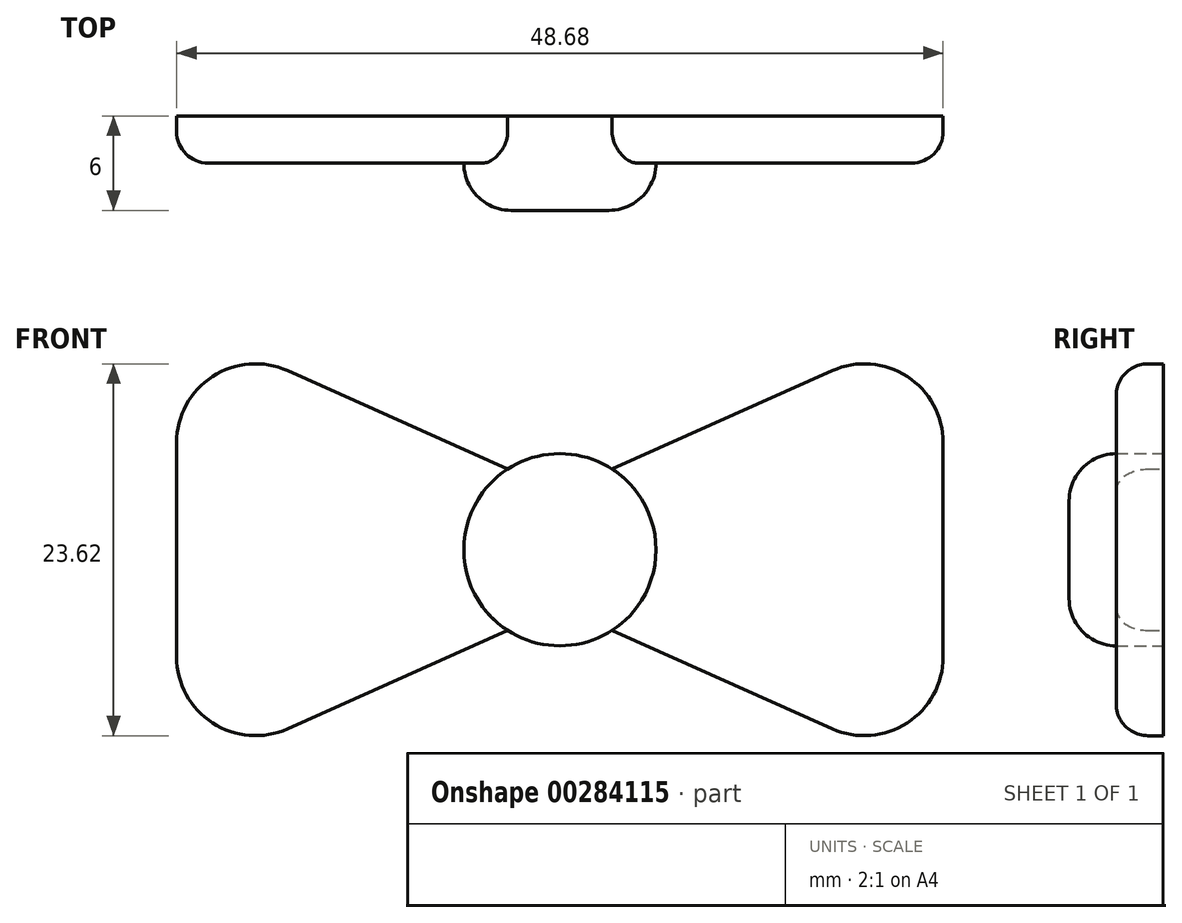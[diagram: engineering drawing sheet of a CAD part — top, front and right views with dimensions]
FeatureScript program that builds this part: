
annotation { "Feature Type Name" : "Feature", "Feature Type Description" : "" }
export const myFeature = defineFeature(function(context is Context, id is Id, definition is map)
    precondition{}
    {
        {
            var Q0;
            Q0=qCreatedBy(makeId("Front.planeOp"),FACE);
            var sketch = newSketch(context, id + "F0", { "sketchPlane" : qUnion([Q0])});
            skCircle(sketch, "E0", {"center": v(0, 0) * mm, "radius": 6.1 * mm});
            skLineSegment(sketch, "E1", {"start": v(0, 4.22) * mm, "end": v(0, -4.55) * mm});
            skSolve(sketch);
        }
        {
            var Q0;
            Q0=qCreatedBy(makeId("Front.planeOp"),FACE);
            var sketch = newSketch(context, id + "F1", { "sketchPlane" : qUnion([Q0])});
            skLineSegment(sketch, "E2", {"start": v(3.18, -5.06) * mm, "end": v(24.34, -14.52) * mm});
            skLineSegment(sketch, "E3.MirrorCS", {"start": v(3.18, 5.06) * mm, "end": v(24.34, 14.52) * mm});
            skLineSegment(sketch, "E4", {"start": v(24.34, 14.52) * mm, "end": v(24.34, -14.52) * mm});
            skLineSegment(sketch, "E5.MirrorCS", {"start": v(-3.18, 5.06) * mm, "end": v(-24.34, 14.52) * mm});
            skLineSegment(sketch, "E6.MirrorCS", {"start": v(-24.34, 14.52) * mm, "end": v(-24.34, -14.52) * mm});
            skLineSegment(sketch, "E7.MirrorCS", {"start": v(-3.18, -5.06) * mm, "end": v(-24.34, -14.52) * mm});
            skLineSegment(sketch, "E8", {"start": v(-3.18, 5.06) * mm, "end": v(3.18, 5.06) * mm});
            skLineSegment(sketch, "E9", {"start": v(3.18, -5.06) * mm, "end": v(-3.18, -5.06) * mm});
            skSolve(sketch);
        }
        {
            var Q0;
            Q0=makeQuery(id+"F0.imprint","IMPRINT",FACE,{"disambiguationData":[TD([[makeQuery(id+"F0.imprint","IMPRINT",EDGE,{"derivedFrom":sQuery(id+"F0.wireOp",EDGE,"E0")}),1.0]])]});
            extrude(context, id + "F2", {"entities" : qUnion([Q0]), "depth" : 6 * mm});
        }
        {
            var Q0;
            Q0=makeQuery(id+"F2.opExtrude","CAP_EDGE",EDGE,{"disambiguationData":[OSD([sQuery(id+"F0.wireOp",EDGE,"E0")])],"isStart":false});
            fillet(context, id + "F3", {"entities" : qUnion([Q0]), "radius" : 3 * mm, "tangentPropagation" : true, "allowEdgeOverflow" : false});
        }
        {
            var Q0;
            Q0=makeQuery(id+"F1.imprint","IMPRINT",FACE,{"disambiguationData":[TD([[makeQuery(id+"F1.imprint","IMPRINT",EDGE,{"derivedFrom":sQuery(id+"F1.wireOp",EDGE,"E2")}),1.0]])]});
            extrude(context, id + "F4", {"entities" : qUnion([Q0]), "operationType" : NewBodyOperationType.ADD, "depth" : 3 * mm});
        }
        {
            var Q0;
            Q0=makeQuery(id+"F4.opExtrude","SWEPT_EDGE",EDGE,{"disambiguationData":[OSD([sQuery(id+"F1.wireOp",EDGE,"E3.MirrorCS"),sQuery(id+"F1.wireOp",EDGE,"E4")])]});
            var Q1;
            Q1=makeQuery(id+"F4.opExtrude","SWEPT_EDGE",EDGE,{"disambiguationData":[OSD([sQuery(id+"F1.wireOp",EDGE,"E2"),sQuery(id+"F1.wireOp",EDGE,"E4")])]});
            var Q2;
            Q2=makeQuery(id+"F4.opExtrude","SWEPT_EDGE",EDGE,{"disambiguationData":[OSD([sQuery(id+"F1.wireOp",EDGE,"E6.MirrorCS"),sQuery(id+"F1.wireOp",EDGE,"E7.MirrorCS")])]});
            var Q3;
            Q3=makeQuery(id+"F4.opExtrude","SWEPT_EDGE",EDGE,{"disambiguationData":[OSD([sQuery(id+"F1.wireOp",EDGE,"E5.MirrorCS"),sQuery(id+"F1.wireOp",EDGE,"E6.MirrorCS")])]});
            fillet(context, id + "F5", {"entities" : qUnion([Q0, Q1, Q2, Q3]), "radius" : 5 * mm, "tangentPropagation" : true, "allowEdgeOverflow" : false});
        }
        {
            var Q0;
            {var subQ0=sQuery(id+"F1.wireOp",EDGE,"E7.MirrorCS");var subQ1=sQuery(id+"F1.wireOp",EDGE,"E6.MirrorCS");var subQ2=sQuery(id+"F1.wireOp",EDGE,"E5.MirrorCS");var subQ3=sQuery(id+"F1.wireOp",EDGE,"E8");var subQ4=sQuery(id+"F1.wireOp",EDGE,"E9");Q0=makeQuery(id+"F5.opFillet","BLEND_EDGE",EDGE,{"blendedFrom":[makeQuery(id+"F4.opExtrude","SWEPT_EDGE",EDGE,{"disambiguationData":[OSD([subQ1,subQ0])]}),makeQuery(id+"F4.boolean.opBoolean","SPLIT",FACE,{"disambiguationData":[TD([makeQuery(id+"F4.opExtrude","SWEPT_FACE",FACE,{"disambiguationData":[OSD([subQ2])]})])],"derivedFrom":makeQuery(id+"F4.opExtrude","CAP_FACE",FACE,{"disambiguationData":[OSD([sQuery(id+"F1.wireOp",EDGE,"E2"),sQuery(id+"F1.wireOp",EDGE,"E3.MirrorCS"),sQuery(id+"F1.wireOp",EDGE,"E4"),subQ2,subQ1,subQ0,subQ3,subQ4])],"isStart":false})})],"blendedInto":[makeQuery(id+"F4.boolean.opBoolean","SPLIT",FACE,{"disambiguationData":[TD([makeQuery(id+"F4.opExtrude","SWEPT_FACE",FACE,{"disambiguationData":[OSD([subQ2])]})])],"derivedFrom":makeQuery(id+"F4.opExtrude","CAP_FACE",FACE,{"disambiguationData":[OSD([sQuery(id+"F1.wireOp",EDGE,"E2"),sQuery(id+"F1.wireOp",EDGE,"E3.MirrorCS"),sQuery(id+"F1.wireOp",EDGE,"E4"),subQ2,subQ1,subQ0,subQ3,subQ4])],"isStart":false})})]});}
            var Q1;
            Q1=makeQuery(id+"F4.opExtrude","CAP_EDGE",EDGE,{"disambiguationData":[OSD([sQuery(id+"F1.wireOp",EDGE,"E3.MirrorCS")])],"isStart":false});
            fillet(context, id + "F6", {"entities" : qUnion([Q0, Q1]), "radius" : 2 * mm, "tangentPropagation" : true, "allowEdgeOverflow" : false});
        }
    });
